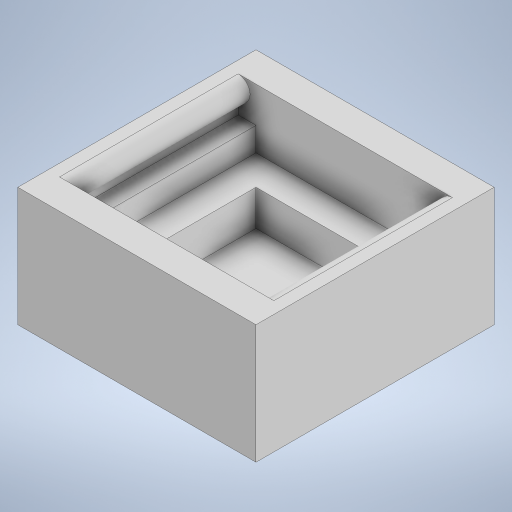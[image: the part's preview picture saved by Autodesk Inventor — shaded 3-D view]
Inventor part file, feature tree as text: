
AUTODESK INVENTOR PART (.ipt)
format: ipt  version: 2023 (Build 270158000, 158)  size: 281,600 bytes
history: native  units: in
note: dims shown in document units (in); Inventor stores cm internally (conversion verified against a paired STEP export)
features: extrude x4, sketch x4, plane x2, shell x1
ambient origin geometry x8: Origin, YZ Plane, XZ Plane, XY Plane, X Axis, Y Axis, Z Axis, Center Point
bodies: Solid1 (feature_tree)
feature tree (11):
  extrude  "Extrusion1"  Depth=1.0in
  shell  "Shell1"  Thickness=0.5in
  sketch  "Sketch2"  dims[d4=0.25in d5=0.75in]
  extrude  "Extrusion2"  Depth=0.75in
  extrude  "Extrusion3"  Depth=0.125in
  plane  "Work Plane1"
  plane  "Work Plane2"
  extrude  "Extrusion4"  Depth=0.4in TaperAngle=0.0deg
  sketch  "Sketch4"  dims[d8=0.125in d9=0.4in d10=0.0in d11=0.25in d12=0.0in d13=-0.5in d14=-0.5in d16=0.1in d17=0.05in d18=0.05in d20=0.1in d21=0.05in d22=0.05in d23=0.05in d24=0.15in d25=0.05in d26=0.15in d27=0.15in d28=0.15in d29=0.15in d30=0.15in d31=0.75in d32=0.0in d33=0.1in d34=0.1in d35=0.05in d36=0.05in d37=0.05in d38=0.05in d39=0.05in d40=0.15in d41=0.05in d42=0.15in d43=0.15in d44=0.15in d45=0.15in d46=0.15in d15=0.0in]
  sketch  "Sketch1"  dims[d0=1.0in d1=1.0in d2=0.5in d3=0.0in]
  sketch  "Sketch3"  dims[d6=0.75in d7=0.125in]
